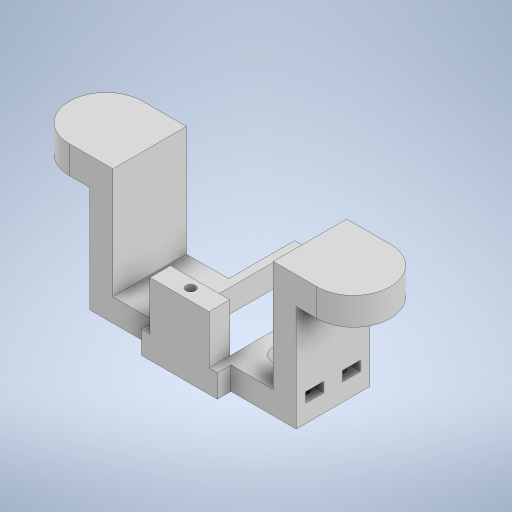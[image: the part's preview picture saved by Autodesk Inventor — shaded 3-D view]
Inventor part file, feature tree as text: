
AUTODESK INVENTOR PART (.ipt)
format: ipt  version: 2023 (Build 270158000, 158)  size: 391,680 bytes
history: native  units: mm
features: sketch x12, extrude x8, hole x4, other x1, mirror x1, projected_geometry x1
ambient origin geometry x8: Origin, YZ Plane, XZ Plane, XY Plane, X Axis, Y Axis, Z Axis, Center Point
bodies: Body1 (feature_tree)
feature tree (27):
  other  "Твердое тело1"
  extrude  "Выдавливание1"  Depth=17.45mm
  extrude  "Выдавливание2"  Depth=16.0mm
  extrude  "Выдавливание3"  Depth=5.0mm TaperAngle=0.0deg
  hole  "Отверстие3"  [1 undecoded]
  extrude  "Выдавливание5"  Depth=5.0mm TaperAngle=0.0deg
  extrude  "Выдавливание6"  Depth=6.0mm TaperAngle=0.0deg
  hole  "Отверстие2"  [1 undecoded]
  mirror  "Зеркальное отражение1"
  extrude  "Выдавливание7"  Depth=8.0mm
  extrude  "Выдавливание8"  Depth=3.9mm
  hole  "Отверстие4"  [1 undecoded]
  extrude  "Выдавливание9"  Depth=8.0mm
  hole  "Отверстие5"  [1 undecoded]
  sketch  "Эскиз1"
  sketch  "Эскиз2"
  sketch  "Эскиз3"
  sketch  "Эскиз4"
  sketch  "Эскиз5"
  sketch  "Эскиз7"
  projected_geometry  "Спроецированная петля4"
  sketch  "Эскиз8"
  sketch  "Эскиз9"
  sketch  "Эскиз10"
  sketch  "Эскиз11"
  sketch  "Эскиз12"
  sketch  "Эскиз13"
note: 4 required parameter values undecoded (feature->parameter linkage not recoverable at this tier; creation-order binding heuristic only, values carry confidence <= 0.55)
